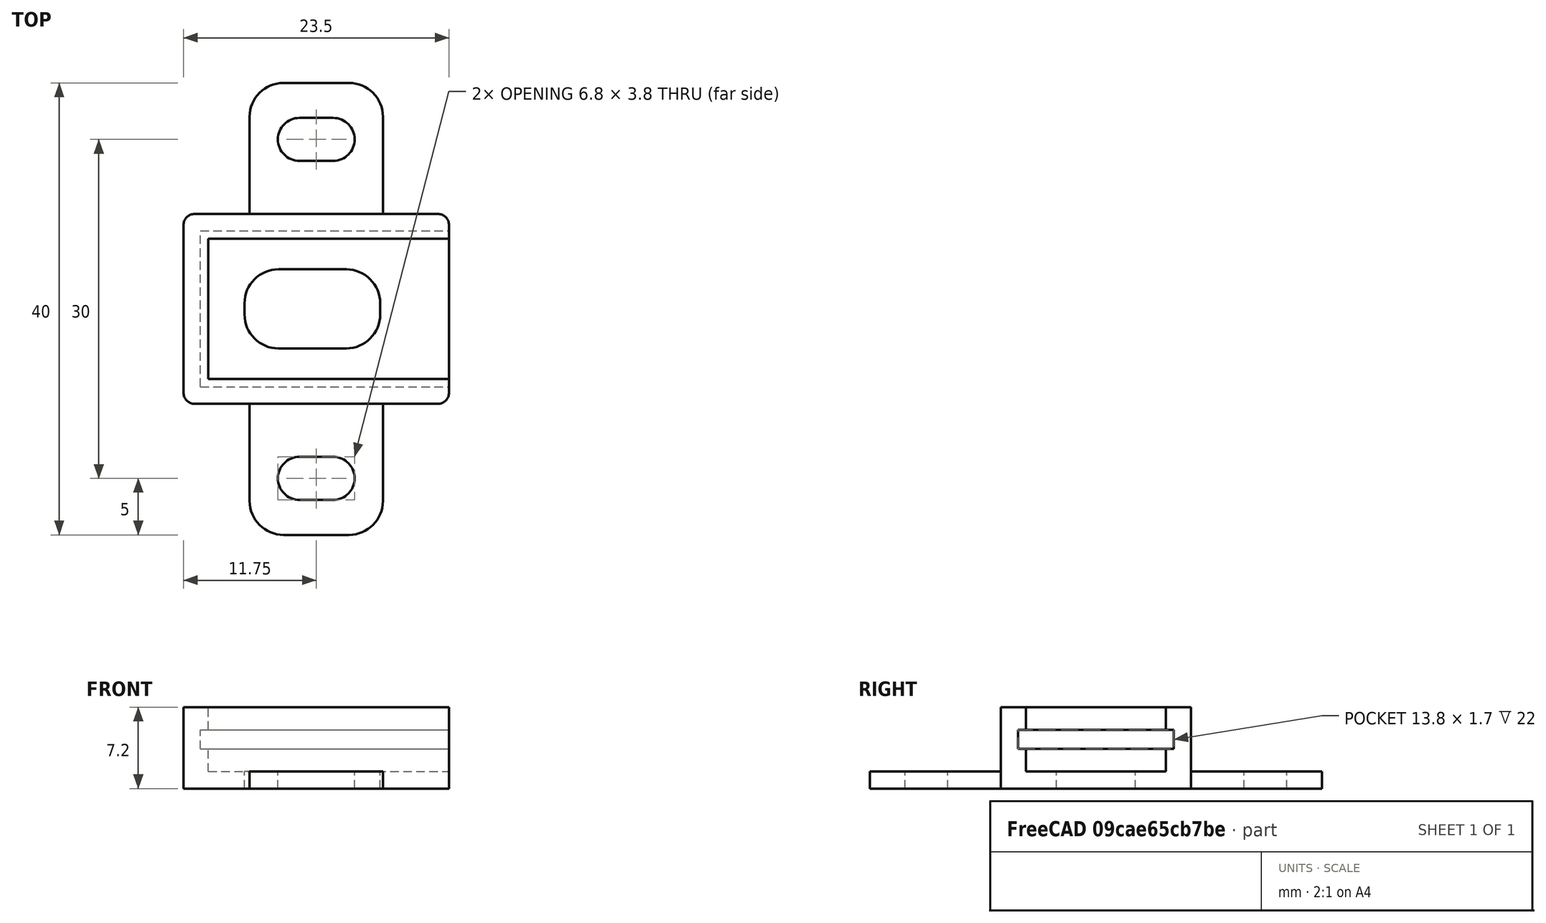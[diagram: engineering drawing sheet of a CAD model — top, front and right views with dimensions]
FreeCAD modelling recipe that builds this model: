
FCSTD DOCUMENT  (FreeCAD 0.19R23578 (Git))
Label: lm336_custom
License: FreeArt
LicenseURL: http://artlibre.org/licence/lal
objects: Part::Box×4, Part::Fillet×2, Part::MultiFuse×2, Spreadsheet::Sheet×1, Part::Feature×1, Part::Cut×1, App::Part×1
note: 10 computed .brp shape members not serialized (recipe doc carries the construction recipe); baked Part::Feature solids carry a one-line shape summary decoded from their .brp

FEATURE [Spreadsheet::Sheet] Spreadsheet  label="p"
  cells = A1=pcb_x; B1(pcb_x)=22; A2=pcb_y; B2(pcb_y)=13.8; A3=pcb_z; B3(pcb_z)=1.7; A4=pcb_under; B4(pcb_under)=2; A5=side_wall; B5(side_wall)=1.5; A6=pcb_side_lane; B6(pcb_side_lane)=0.7; A7=bottom_wall; B7(bottom_wall)=1.5; A8=pcb_above; B8(pcb_above)=2; A9=bottom_hole_x; B9(bottom_hole_x)=12; A10=bottom_hole_y; B10(bottom_hole_y)=7
FEATURE [Part::Box] Box  label="external cube"
  AttacherType = Attacher::AttachEngine3D
  Height = 7.2
  Length = 23.5
  Width = 16.8
  expr: Height = <<p>>.bottom_wall + <<p>>.pcb_under + <<p>>.pcb_z + <<p>>.pcb_above
  expr: Width = <<p>>.pcb_y + 2 * <<p>>.side_wall
  expr: Length = <<p>>.pcb_x + <<p>>.side_wall
FEATURE [Part::Box] Box006  label="internal cube"
  AttacherType = Attacher::AttachEngine3D
  Height = 5.7
  Length = 22.1
  Placement = pos=(2.2,2.2,1.5) rot=(0,0,1;0rad)
  Width = 12.4
  expr: .Placement.Base.y = <<p>>.side_wall + <<p>>.pcb_side_lane
  expr: .Placement.Base.x = <<p>>.side_wall + <<p>>.pcb_side_lane
  expr: .Placement.Base.z = <<p>>.bottom_wall
  expr: Height = <<p>>.pcb_under + <<p>>.pcb_z + <<p>>.pcb_above
  expr: Width = <<p>>.pcb_y - 2 * <<p>>.pcb_side_lane
  expr: Length = <<p>>.pcb_x - 2 * <<p>>.pcb_side_lane + <<p>>.side_wall
FEATURE [Part::Box] Box007  label="pcb extract cube"
  AttacherType = Attacher::AttachEngine3D
  Height = 1.7
  Length = 22
  Placement = pos=(1.5,1.5,3.5) rot=(0,0,1;0rad)
  Width = 13.8
  expr: .Placement.Base.y = <<p>>.side_wall
  expr: .Placement.Base.x = <<p>>.side_wall
  expr: Length = <<p>>.pcb_x
  expr: Width = <<p>>.pcb_y
  expr: .Placement.Base.z = <<p>>.bottom_wall + <<p>>.pcb_under
  expr: Height = <<p>>.pcb_z
FEATURE [Part::Fillet] Fillet  label="external fillet"
  Base = -> Box
  Edges = 4 edges r=1: [Edge1,Edge3,Edge5,Edge7]
FEATURE [Part::Box] Box008  label="bottom hole"
  AttacherType = Attacher::AttachEngine3D
  Height = 10
  Length = 12
  Placement = pos=(5.4,4.9,0) rot=(0,0,1;0rad)
  Width = 7
  expr: Length = <<p>>.bottom_hole_x
  expr: Width = <<p>>.bottom_hole_y
  expr: .Placement.Base.x = (<<p>>.pcb_x + <<p>>.side_wall - <<p>>.pcb_side_lane - <<p>>.bottom_hole_x) / 2
  expr: .Placement.Base.y = (<<p>>.pcb_y + 2 * <<p>>.side_wall - <<p>>.bottom_hole_y) / 2
FEATURE [Part::Fillet] Fillet001  label="bottom hole fillet"
  Base = -> Box008
  Edges = 4 edges r=3: [Edge1,Edge3,Edge5,Edge7]
FEATURE [Part::MultiFuse] Fusion  label="extract fusion"
  Shapes = -> [Box006,Box007,Fillet001]
FEATURE [Part::Feature] Cut002002  label="attach plane y dir002"
  Placement = pos=(5.85,-11.6,0) rot=(0,0,1;0rad)
  shape: bbox 11.8 x 40 x 1.5 mm, 20 faces (baked)
FEATURE [Part::MultiFuse] Fusion001  label="solid fusion"
  Shapes = -> [Fillet,Cut002002]
FEATURE [Part::Cut] Cut  label="body cut"
  Base = -> Fusion001
  Tool = -> Fusion
FEATURE [App::Part] Part  label="pcb box part"
  Group = -> [Box,Fillet,Fusion001,Fusion,Box007,Box006,Cut]
  Origin = -> Origin
